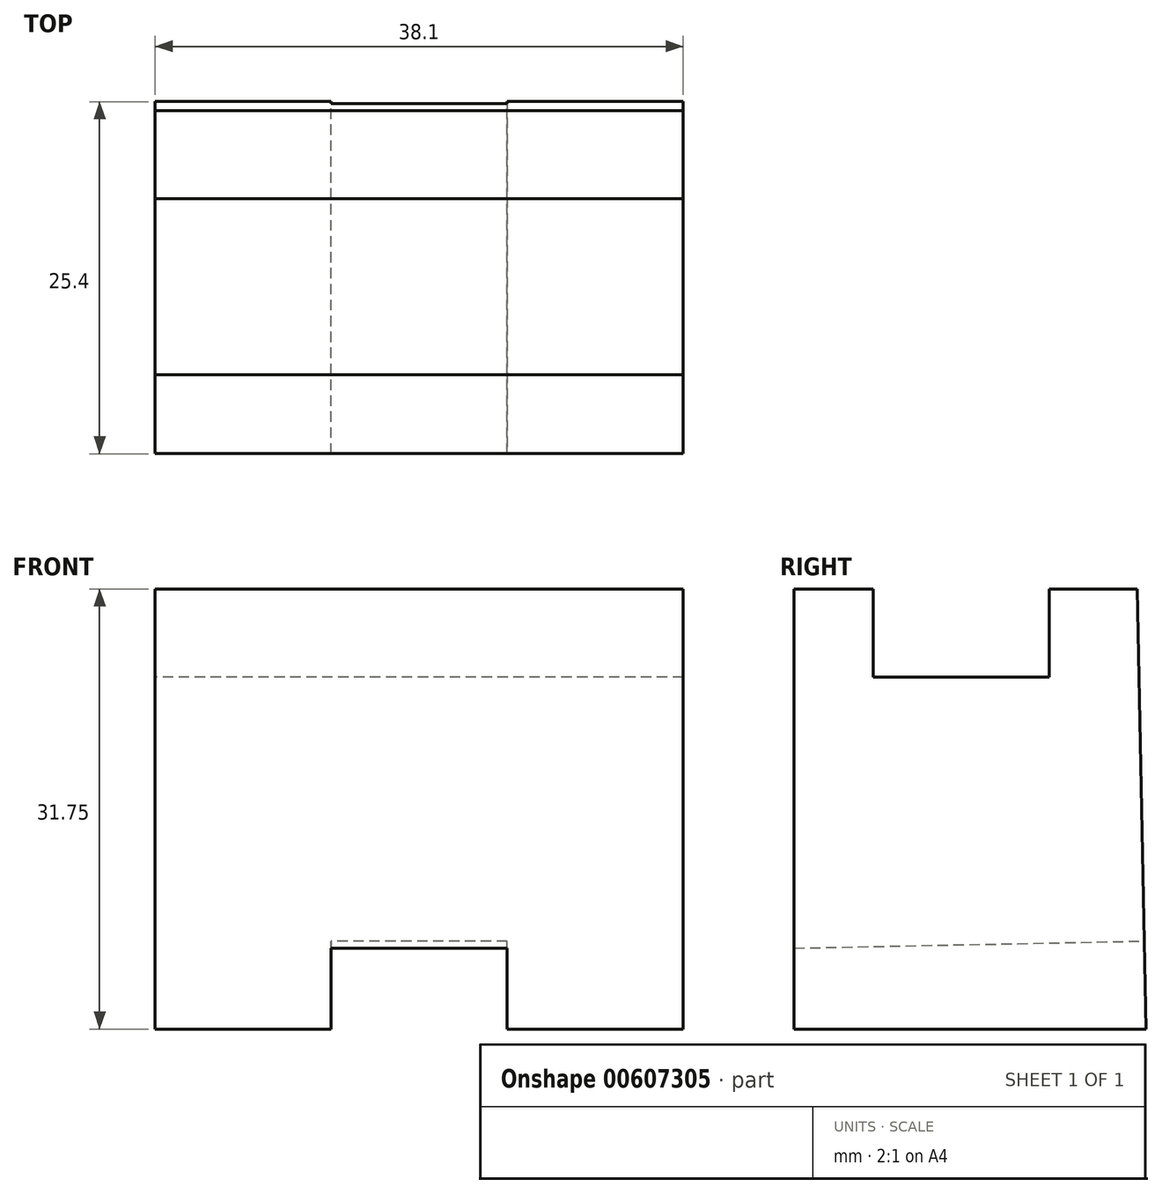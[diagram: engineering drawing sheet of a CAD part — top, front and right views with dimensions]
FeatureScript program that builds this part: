
annotation { "Feature Type Name" : "Feature", "Feature Type Description" : "" }
export const myFeature = defineFeature(function(context is Context, id is Id, definition is map)
    precondition{}
    {
        {
            var Q0;
            Q0=qCreatedBy(makeId("Right.planeOp"),FACE);
            var sketch = newSketch(context, id + "F0", { "sketchPlane" : qUnion([Q0])});
            skLineSegment(sketch, "E0", {"start": v(-18.4, -14.7) * mm, "end": v(7, -14.7) * mm});
            skLineSegment(sketch, "E1", {"start": v(-18.4, -14.7) * mm, "end": v(-18.4, 17.05) * mm});
            skLineSegment(sketch, "E2", {"start": v(-18.4, 17.05) * mm, "end": v(-12.7, 17.05) * mm});
            skLineSegment(sketch, "E3", {"start": v(-12.7, 17.05) * mm, "end": v(-12.7, 10.7) * mm});
            skLineSegment(sketch, "E4", {"start": v(-12.7, 10.7) * mm, "end": v(0, 10.7) * mm});
            skLineSegment(sketch, "E5", {"start": v(0, 10.7) * mm, "end": v(0, 17.05) * mm});
            skLineSegment(sketch, "E6", {"start": v(0, 17.05) * mm, "end": v(6.35, 17.05) * mm});
            skLineSegment(sketch, "E7", {"start": v(6.35, 17.05) * mm, "end": v(7, -14.7) * mm});
            skSolve(sketch);
        }
        {
            var Q0;
            Q0 = qSketchRegion(id + "F0", true);
            extrude(context, id + "F1", {"entities" : qUnion([Q0]), "depth" : 38.1 * mm, "offsetDistance" : 25.4 * mm});
        }
        {
            var Q0;
            Q0=makeQuery(id+"F1.opExtrude","SWEPT_FACE",FACE,{"disambiguationData":[OSD([sQuery(id+"F0.wireOp",EDGE,"E7")])]});
            var sketch = newSketch(context, id + "F2", { "sketchPlane" : qUnion([Q0])});
            skLineSegment(sketch, "E8", {"start": v(-38.1, -14.84) * mm, "end": v(-25.4, -14.84) * mm});
            skLineSegment(sketch, "E9", {"start": v(-25.4, -14.84) * mm, "end": v(-25.4, -8.49) * mm});
            skLineSegment(sketch, "E10", {"start": v(-25.4, -8.49) * mm, "end": v(-12.7, -8.49) * mm});
            skLineSegment(sketch, "E11", {"start": v(-12.7, -8.49) * mm, "end": v(-12.7, -14.84) * mm});
            skLineSegment(sketch, "E12", {"start": v(-12.7, -14.84) * mm, "end": v(-25.4, -14.84) * mm});
            skSolve(sketch);
        }
        {
            var Q0;
            Q0=makeQuery(id+"F2.imprint","IMPRINT",FACE,{"disambiguationData":[TD([[makeQuery(id+"F2.imprint","IMPRINT",EDGE,{"derivedFrom":sQuery(id+"F2.wireOp",EDGE,"E9")}),-1.0]])]});
            extrude(context, id + "F3", {"entities" : qUnion([Q0]), "operationType" : NewBodyOperationType.REMOVE, "oppositeDirection" : true, "depth" : 25.4 * mm, "offsetDistance" : 25.4 * mm});
        }
    });
